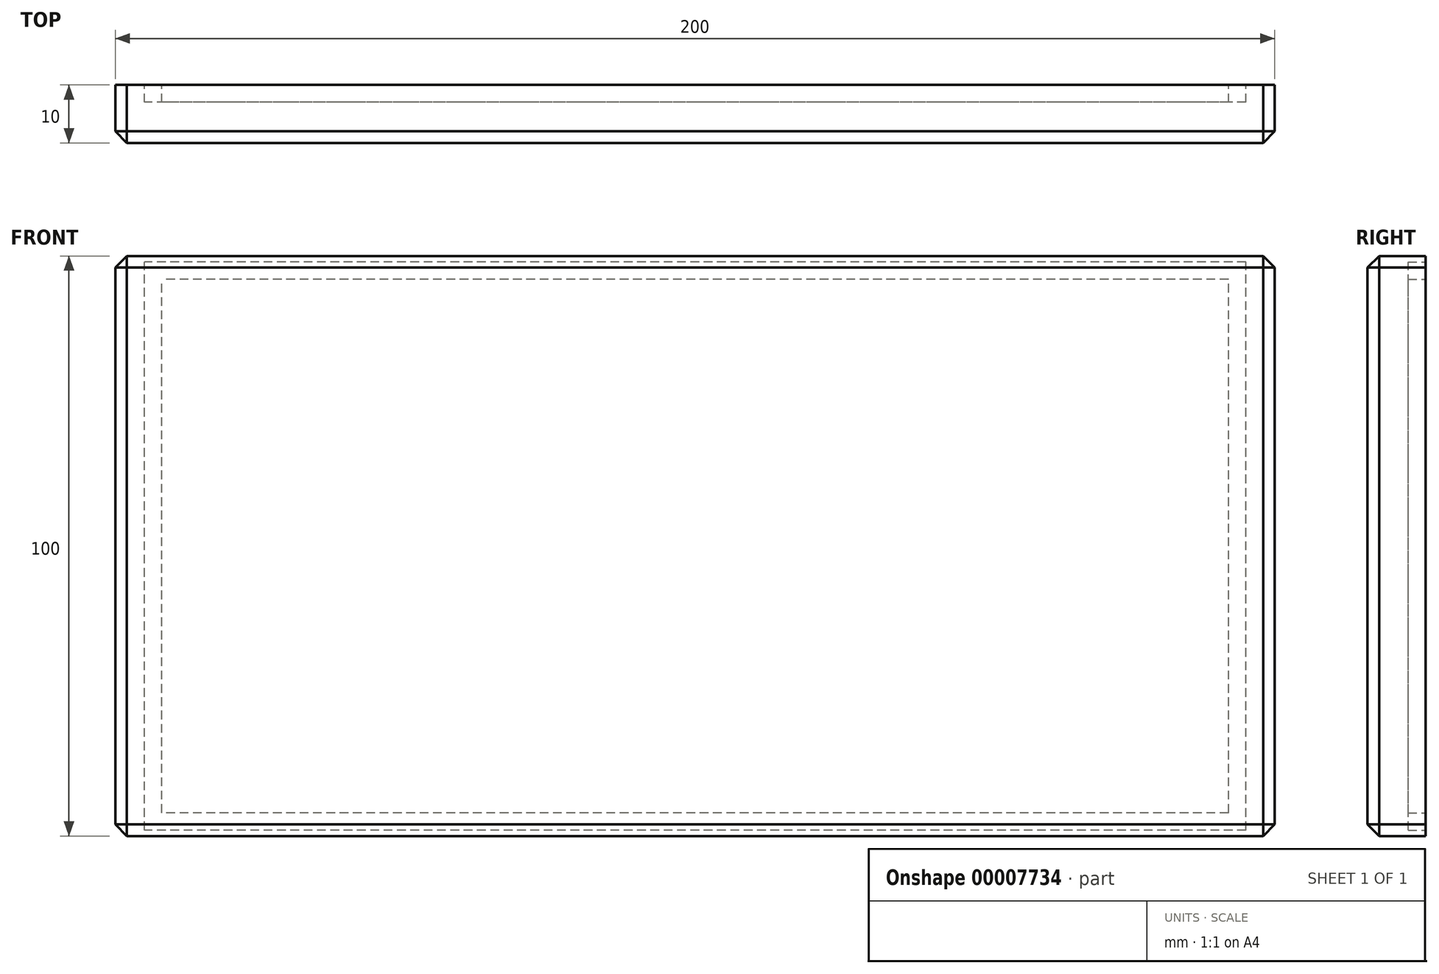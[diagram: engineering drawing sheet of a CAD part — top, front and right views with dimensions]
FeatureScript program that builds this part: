
annotation { "Feature Type Name" : "Feature", "Feature Type Description" : "" }
export const myFeature = defineFeature(function(context is Context, id is Id, definition is map)
    precondition{}
    {
        {
            var Q0;
            Q0=qCreatedBy(makeId("Front.planeOp"),FACE);
            var sketch = newSketch(context, id + "F0", { "sketchPlane" : qUnion([Q0])});
            skLineSegment(sketch, "E0.bottom", {"start": v(0, 0) * mm, "end": v(200, 0) * mm});
            skLineSegment(sketch, "E0.top", {"start": v(0, 100) * mm, "end": v(200, 100) * mm});
            skLineSegment(sketch, "E0.left", {"start": v(0, 0) * mm, "end": v(0, 100) * mm});
            skLineSegment(sketch, "E0.right", {"start": v(200, 0) * mm, "end": v(200, 100) * mm});
            skSolve(sketch);
        }
        {
            var Q0;
            Q0=makeQuery(id+"F0.imprint","IMPRINT",FACE,{"disambiguationData":[TD([[makeQuery(id+"F0.imprint","IMPRINT",EDGE,{"derivedFrom":sQuery(id+"F0.wireOp",EDGE,"E0.bottom")}),1.0]])]});
            extrude(context, id + "F1", {"entities" : qUnion([Q0]), "depth" : 10 * mm});
        }
        {
            var Q0;
            Q0=makeQuery(id+"F1.opExtrude","CAP_FACE",FACE,{"disambiguationData":[OSD([sQuery(id+"F0.wireOp",EDGE,"E0.bottom"),sQuery(id+"F0.wireOp",EDGE,"E0.top"),sQuery(id+"F0.wireOp",EDGE,"E0.left"),sQuery(id+"F0.wireOp",EDGE,"E0.right")])],"isStart":true});
            var sketch = newSketch(context, id + "F2", { "sketchPlane" : qUnion([Q0])});
            skLineSegment(sketch, "E1.bottom", {"start": v(-195, 1) * mm, "end": v(-5, 1) * mm});
            skLineSegment(sketch, "E1.top", {"start": v(-195, 99) * mm, "end": v(-5, 99) * mm});
            skLineSegment(sketch, "E1.left", {"start": v(-195, 1) * mm, "end": v(-195, 99) * mm});
            skLineSegment(sketch, "E1.right", {"start": v(-5, 1) * mm, "end": v(-5, 99) * mm});
            skLineSegment(sketch, "E2.bottom", {"start": v(-192, 4) * mm, "end": v(-8, 4) * mm});
            skLineSegment(sketch, "E2.top", {"start": v(-192, 96) * mm, "end": v(-8, 96) * mm});
            skLineSegment(sketch, "E2.left", {"start": v(-192, 4) * mm, "end": v(-192, 96) * mm});
            skLineSegment(sketch, "E2.right", {"start": v(-8, 4) * mm, "end": v(-8, 96) * mm});
            skSolve(sketch);
        }
        {
            var Q0;
            Q0=makeQuery(id+"F2.imprint","IMPRINT",FACE,{"disambiguationData":[TD([[makeQuery(id+"F2.imprint","IMPRINT",EDGE,{"derivedFrom":sQuery(id+"F2.wireOp",EDGE,"E1.bottom")}),1.0]])]});
            extrude(context, id + "F3", {"entities" : qUnion([Q0]), "operationType" : NewBodyOperationType.REMOVE, "oppositeDirection" : true, "depth" : 3 * mm});
        }
        {
            var Q0;
            Q0=makeQuery(id+"F1.opExtrude","CAP_EDGE",EDGE,{"disambiguationData":[OSD([sQuery(id+"F0.wireOp",EDGE,"E0.top")])],"isStart":false});
            var Q1;
            Q1=makeQuery(id+"F1.opExtrude","CAP_EDGE",EDGE,{"disambiguationData":[OSD([sQuery(id+"F0.wireOp",EDGE,"E0.right")])],"isStart":false});
            var Q2;
            Q2=makeQuery(id+"F1.opExtrude","CAP_EDGE",EDGE,{"disambiguationData":[OSD([sQuery(id+"F0.wireOp",EDGE,"E0.bottom")])],"isStart":false});
            var Q3;
            Q3=makeQuery(id+"F1.opExtrude","CAP_EDGE",EDGE,{"disambiguationData":[OSD([sQuery(id+"F0.wireOp",EDGE,"E0.left")])],"isStart":false});
            var Q4;
            Q4=makeQuery(id+"F1.opExtrude","SWEPT_EDGE",EDGE,{"disambiguationData":[OSD([sQuery(id+"F0.wireOp",EDGE,"E0.top"),sQuery(id+"F0.wireOp",EDGE,"E0.left")])]});
            var Q5;
            Q5=makeQuery(id+"F1.opExtrude","SWEPT_EDGE",EDGE,{"disambiguationData":[OSD([sQuery(id+"F0.wireOp",EDGE,"E0.top"),sQuery(id+"F0.wireOp",EDGE,"E0.right")])]});
            var Q6;
            Q6=makeQuery(id+"F1.opExtrude","SWEPT_EDGE",EDGE,{"disambiguationData":[OSD([sQuery(id+"F0.wireOp",EDGE,"E0.bottom"),sQuery(id+"F0.wireOp",EDGE,"E0.right")])]});
            var Q7;
            Q7=makeQuery(id+"F1.opExtrude","SWEPT_EDGE",EDGE,{"disambiguationData":[OSD([sQuery(id+"F0.wireOp",EDGE,"E0.bottom"),sQuery(id+"F0.wireOp",EDGE,"E0.left")])]});
            chamfer(context, id + "F4", {"entities" : qUnion([Q0, Q1, Q2, Q3, Q4, Q5, Q6, Q7]), "width" : 2 * mm});
        }
    });
